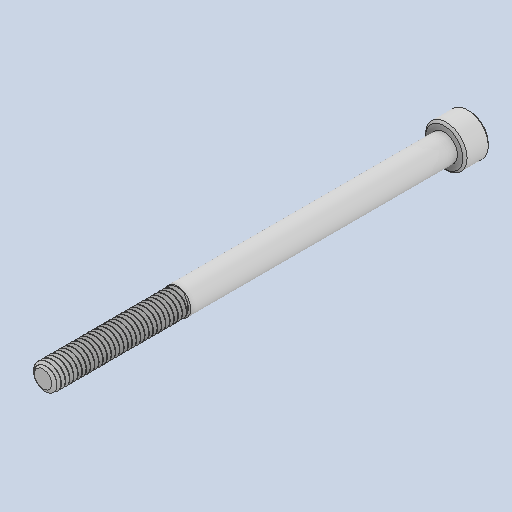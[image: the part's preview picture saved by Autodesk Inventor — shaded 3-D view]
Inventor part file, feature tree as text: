
AUTODESK INVENTOR PART (.ipt)
format: ipt  version: 2023 (Build 270158030, 158C)  size: 931,840 bytes
history: native  units: in
note: dims shown in document units (in); Inventor stores cm internally (conversion verified against a paired STEP export)
features: chamfer x1
ambient origin geometry x8: Origin, YZ Plane, XZ Plane, XY Plane, X Axis, Y Axis, Z Axis, Center Point
bodies: Solid1 (feature_tree)
feature tree (1):
  chamfer  "Chamfer1"  [1 undecoded]
note: 1 required parameter value undecoded (feature->parameter linkage not recoverable at this tier; creation-order binding heuristic only, values carry confidence <= 0.55)
